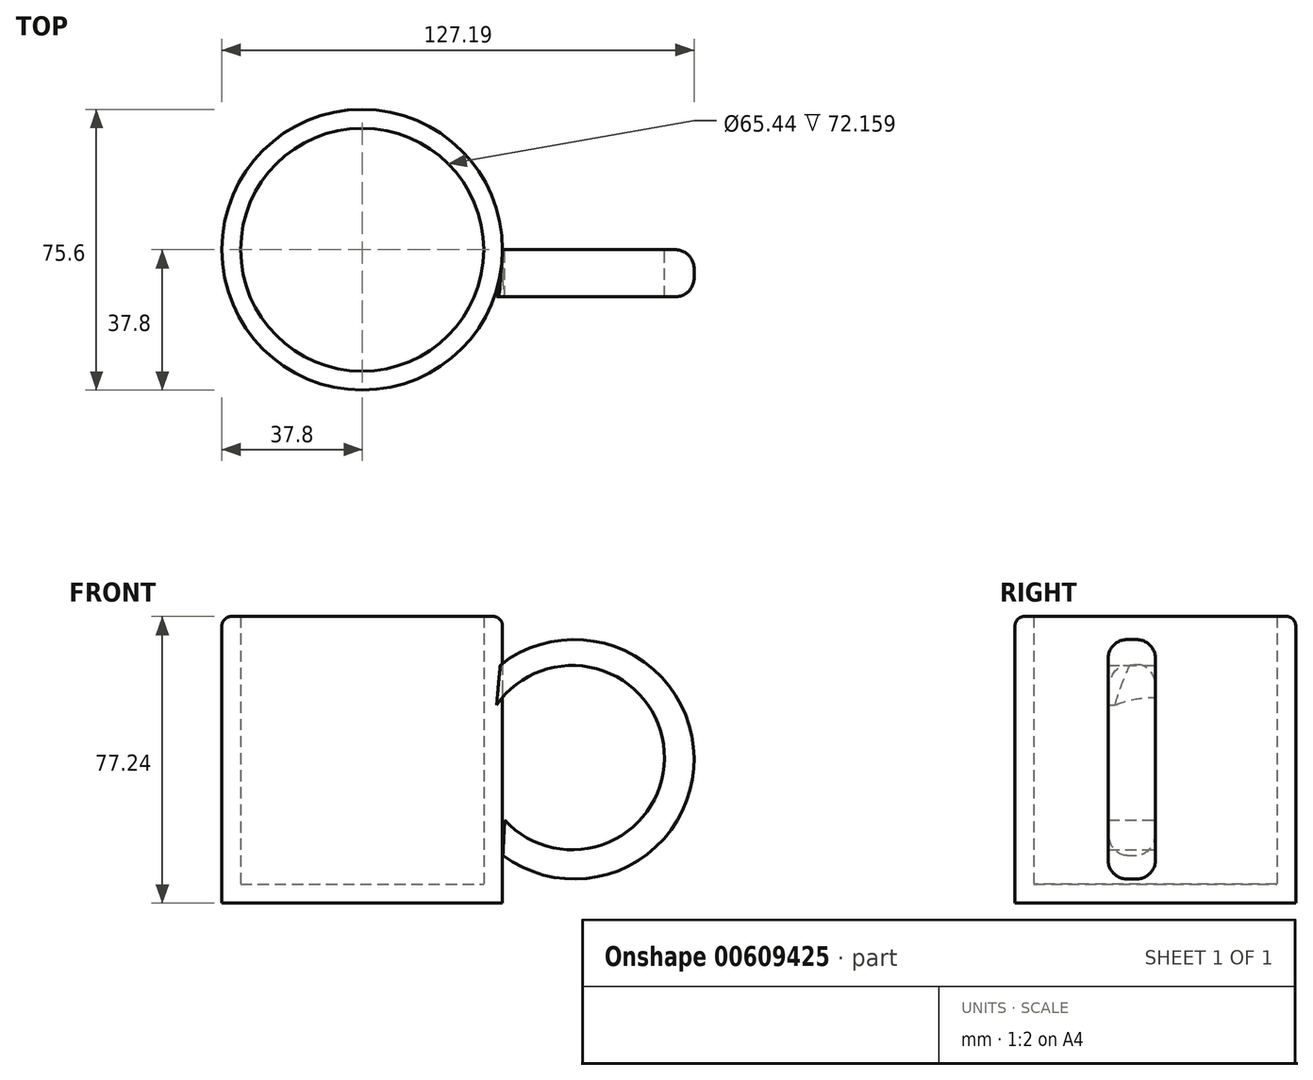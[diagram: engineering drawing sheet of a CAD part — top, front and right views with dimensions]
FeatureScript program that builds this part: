
annotation { "Feature Type Name" : "Feature", "Feature Type Description" : "" }
export const myFeature = defineFeature(function(context is Context, id is Id, definition is map)
    precondition{}
    {
        {
            var Q0;
            Q0=qCreatedBy(makeId("Front.planeOp"),FACE);
            var sketch = newSketch(context, id + "F0", { "sketchPlane" : qUnion([Q0])});
            skLineSegment(sketch, "E0", {"start": v(0, 0) * mm, "end": v(-37.8, 0) * mm});
            skLineSegment(sketch, "E1", {"start": v(-37.8, 0) * mm, "end": v(-37.8, 77.24) * mm});
            skLineSegment(sketch, "E2", {"start": v(0, 0) * mm, "end": v(0, 77.24) * mm});
            skLineSegment(sketch, "E3", {"start": v(0, 77.24) * mm, "end": v(-37.8, 77.24) * mm});
            skSolve(sketch);
        }
        {
            var Q0;
            Q0=makeQuery(id+"F0.imprint","IMPRINT",FACE,{"disambiguationData":[TD([[makeQuery(id+"F0.imprint","IMPRINT",EDGE,{"derivedFrom":sQuery(id+"F0.wireOp",EDGE,"E0")}),-1.0]])]});
            var Q1;
            Q1=sQuery(id+"F0.wireOp",EDGE,"E2");
            revolve(context, id + "F1", {"entities" : qUnion([Q0]), "axis" : qUnion([Q1]), "revolveType" : RevolveType.FULL});
        }
        {
            var Q0;
            Q0=makeQuery(id+"F1.opRevolve","SWEPT_FACE",FACE,{"disambiguationData":[OSD([sQuery(id+"F0.wireOp",EDGE,"E3")])]});
            shell(context, id + "F2", {"entities" : qUnion([Q0]), "thickness" : 5.08 * mm});
        }
        {
            var Q0;
            Q0=makeQuery(id+"F1.opRevolve","SWEPT_EDGE",EDGE,{"disambiguationData":[OSD([sQuery(id+"F0.wireOp",EDGE,"E1"),sQuery(id+"F0.wireOp",EDGE,"E3")])]});
            fillet(context, id + "F3", {"entities" : qUnion([Q0]), "radius" : 2.54 * mm, "tangentPropagation" : true, "allowEdgeOverflow" : false});
        }
        {
            var Q0;
            Q0=qCreatedBy(makeId("Front.planeOp"),FACE);
            var sketch = newSketch(context, id + "F4", { "sketchPlane" : qUnion([Q0])});
            skArc(sketch, "E4", {"start": v(37.9, 12.86) * mm, "mid": v(89.39, 39.22) * mm, "end": v(37.18, 64.12) * mm});
            skArc(sketch, "E5", {"start": v(38.34, 22.38) * mm, "mid": v(81.35, 40.93) * mm, "end": v(36.2, 53.38) * mm});
            skLineSegment(sketch, "E6", {"start": v(38.34, 22.38) * mm, "end": v(37.9, 12.86) * mm});
            skLineSegment(sketch, "E7", {"start": v(36.2, 53.38) * mm, "end": v(37.18, 64.12) * mm});
            skSolve(sketch);
        }
        {
            var Q0;
            Q0 = qSketchRegion(id + "F4", true);
            extrude(context, id + "F5", {"entities" : qUnion([Q0]), "operationType" : NewBodyOperationType.ADD, "depth" : 12.7 * mm, "offsetDistance" : 25.4 * mm});
        }
        {
            var Q0;
            Q0=makeQuery(id+"F5.opExtrude","CAP_EDGE",EDGE,{"disambiguationData":[OSD([sQuery(id+"F4.wireOp",EDGE,"E4")])],"isStart":true});
            var Q1;
            Q1=makeQuery(id+"F5.opExtrude","CAP_EDGE",EDGE,{"disambiguationData":[OSD([sQuery(id+"F4.wireOp",EDGE,"E4")])],"isStart":false});
            fillet(context, id + "F6", {"entities" : qUnion([Q0, Q1]), "radius" : 5.08 * mm, "tangentPropagation" : true, "allowEdgeOverflow" : false});
        }
    });
